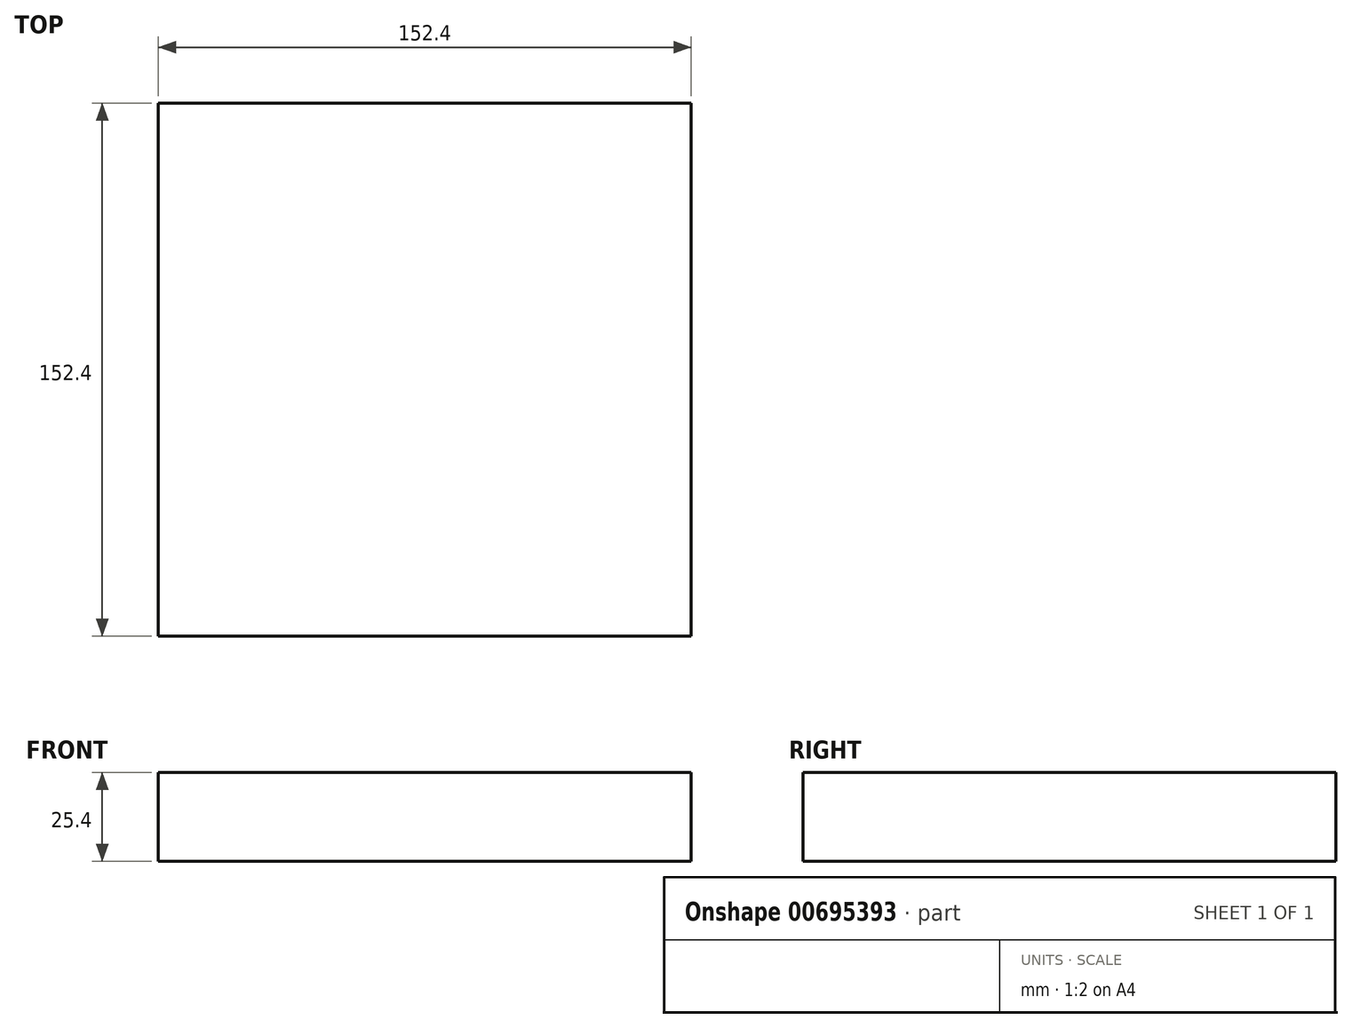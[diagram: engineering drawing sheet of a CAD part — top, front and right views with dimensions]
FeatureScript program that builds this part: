
annotation { "Feature Type Name" : "Feature", "Feature Type Description" : "" }
export const myFeature = defineFeature(function(context is Context, id is Id, definition is map)
    precondition{}
    {
        {
            var Q0;
            Q0=qCreatedBy(makeId("Top.planeOp"),FACE);
            var sketch = newSketch(context, id + "F0", { "sketchPlane" : qUnion([Q0])});
            skLineSegment(sketch, "E0.bottom", {"start": v(-76.4, 76.56) * mm, "end": v(76, 76.56) * mm});
            skLineSegment(sketch, "E0.top", {"start": v(-76.4, -75.84) * mm, "end": v(76, -75.84) * mm});
            skLineSegment(sketch, "E0.left", {"start": v(-76.4, 76.56) * mm, "end": v(-76.4, -75.84) * mm});
            skLineSegment(sketch, "E0.right", {"start": v(76, 76.56) * mm, "end": v(76, -75.84) * mm});
            skSolve(sketch);
        }
        {
            var Q0;
            Q0=makeQuery(id+"F0.imprint","IMPRINT",FACE,{"disambiguationData":[TD([[makeQuery(id+"F0.imprint","IMPRINT",EDGE,{"derivedFrom":sQuery(id+"F0.wireOp",EDGE,"E0.bottom")}),-1.0]])]});
            extrude(context, id + "F1", {"entities" : qUnion([Q0]), "depth" : 25.4 * mm, "offsetDistance" : 25.4 * mm});
        }
    });
